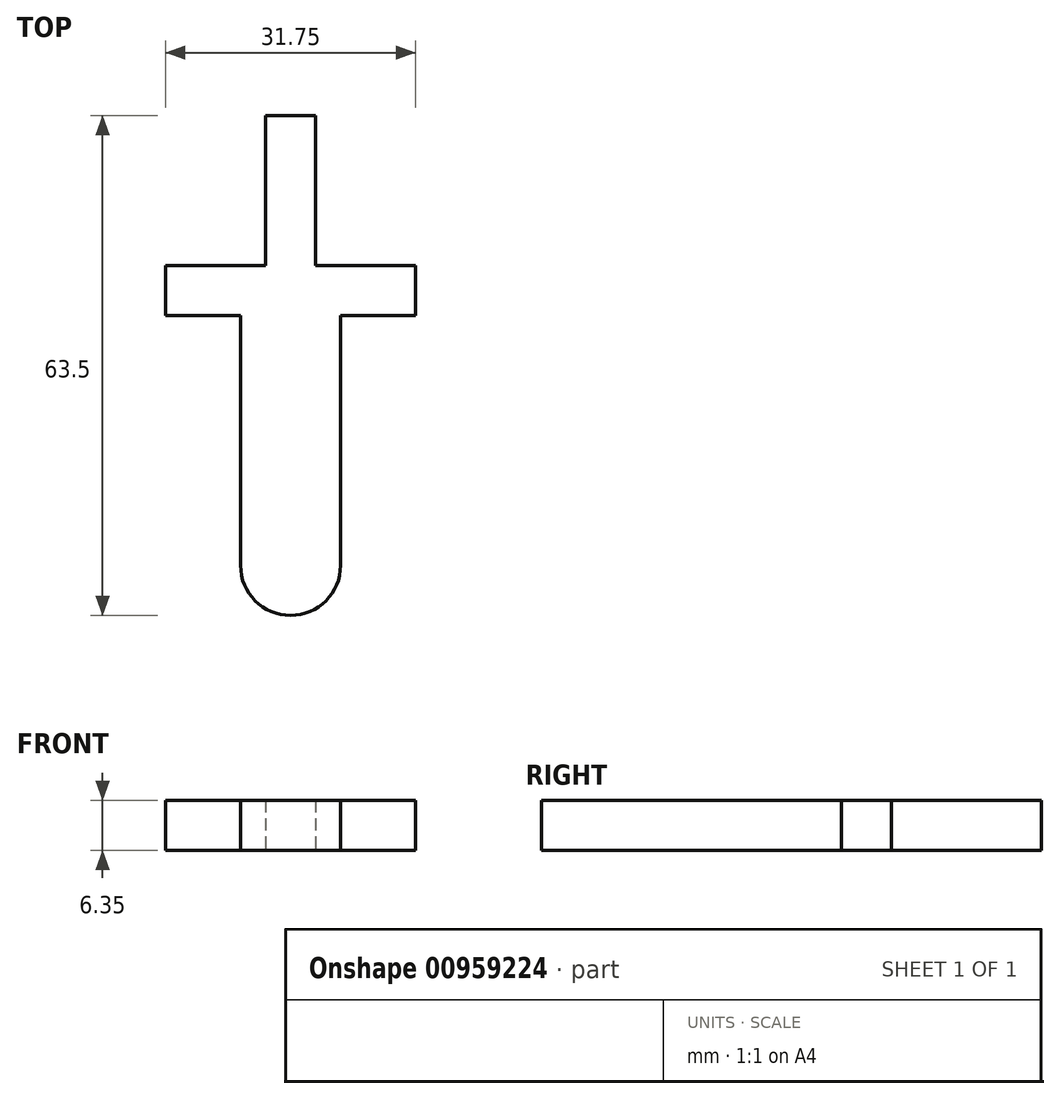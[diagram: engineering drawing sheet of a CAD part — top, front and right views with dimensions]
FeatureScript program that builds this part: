
annotation { "Feature Type Name" : "Feature", "Feature Type Description" : "" }
export const myFeature = defineFeature(function(context is Context, id is Id, definition is map)
    precondition{}
    {
        {
            var Q0;
            Q0=qCreatedBy(makeId("Top.planeOp"),FACE);
            var sketch = newSketch(context, id + "F0", { "sketchPlane" : qUnion([Q0])});
            skLineSegment(sketch, "E0.top", {"start": v(0, 19.05) * mm, "end": v(-6.35, 19.05) * mm});
            skLineSegment(sketch, "E0.left", {"start": v(0, 0) * mm, "end": v(0, 19.05) * mm});
            skLineSegment(sketch, "E0.right", {"start": v(-6.35, 0) * mm, "end": v(-6.35, 19.05) * mm});
            skLineSegment(sketch, "E1", {"start": v(-6.35, 0) * mm, "end": v(-19.05, 0) * mm});
            skLineSegment(sketch, "E2", {"start": v(-19.05, 0) * mm, "end": v(-19.05, -6.35) * mm});
            skLineSegment(sketch, "E3", {"start": v(-19.05, -6.35) * mm, "end": v(-9.52, -6.35) * mm});
            skLineSegment(sketch, "E4", {"start": v(-9.52, -6.35) * mm, "end": v(-9.52, -38.1) * mm});
            skLineSegment(sketch, "E5", {"start": v(-3.17, -44.45) * mm, "end": v(-3.17, -44.45) * mm});
            skLineSegment(sketch, "E6", {"start": v(3.18, -38.1) * mm, "end": v(3.18, -6.35) * mm});
            skLineSegment(sketch, "E7", {"start": v(3.18, -6.35) * mm, "end": v(12.7, -6.35) * mm});
            skLineSegment(sketch, "E8", {"start": v(12.7, -6.35) * mm, "end": v(12.7, 0) * mm});
            skLineSegment(sketch, "E9", {"start": v(12.7, 0) * mm, "end": v(0, 0) * mm});
            skPoint(sketch, "E10.visualSharp", {"position": v(-9.52, -44.45) * mm});
            skArc(sketch, "E10.filletArc", {"start": v(-9.52, -38.1) * mm, "mid": v(-7.67, -42.6) * mm, "end": v(-3.17, -44.45) * mm});
            skPoint(sketch, "E11.visualSharp", {"position": v(3.18, -44.45) * mm});
            skArc(sketch, "E11.filletArc", {"start": v(-3.17, -44.45) * mm, "mid": v(1.32, -42.6) * mm, "end": v(3.18, -38.1) * mm});
            skSolve(sketch);
        }
        {
            var Q0;
            Q0=makeQuery(id+"F0.imprint","IMPRINT",FACE,{"disambiguationData":[TD([[makeQuery(id+"F0.imprint","IMPRINT",EDGE,{"derivedFrom":sQuery(id+"F0.wireOp",EDGE,"E0.top")}),1.0]])]});
            extrude(context, id + "F1", {"entities" : qUnion([Q0]), "depth" : 6.35 * mm, "offsetDistance" : 25.4 * mm});
        }
    });
